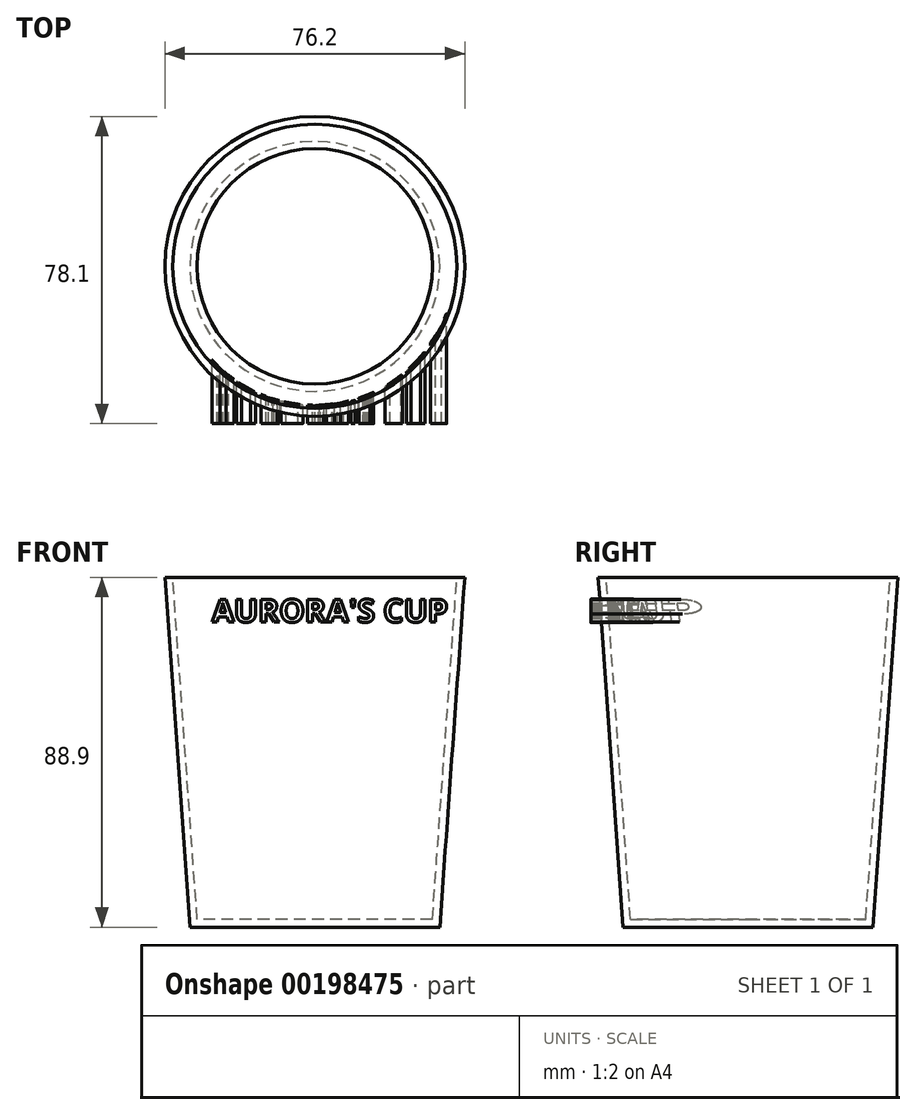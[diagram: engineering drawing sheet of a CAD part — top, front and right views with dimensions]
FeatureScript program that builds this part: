
annotation { "Feature Type Name" : "Feature", "Feature Type Description" : "" }
export const myFeature = defineFeature(function(context is Context, id is Id, definition is map)
    precondition{}
    {
        {
            var Q0;
            Q0=qCreatedBy(makeId("Top.planeOp"),FACE);
            var sketch = newSketch(context, id + "F0", { "sketchPlane" : qUnion([Q0])});
            skCircle(sketch, "E0", {"center": v(0, 0) * mm, "radius": 31.75 * mm});
            skSolve(sketch);
        }
        {
            var Q0;
            Q0=qCreatedBy(makeId("Top.planeOp"),FACE);
            cPlane(context, id + "F1", {"entities" : qUnion([Q0]), "cplaneType" : CPlaneType.OFFSET, "offset" : 88.9 * mm, "width" : 152.4 * mm, "height" : 152.4 * mm});
        }
        {
            var Q0;
            Q0=qCreatedBy(id+"F1.planeOp",FACE);
            var sketch = newSketch(context, id + "F2", { "sketchPlane" : qUnion([Q0])});
            skCircle(sketch, "E1", {"center": v(0, 0) * mm, "radius": 38.1 * mm});
            skSolve(sketch);
        }
        {
            var Q0;
            Q0 = qSketchRegion(id + "F0", true);
            var Q1;
            Q1 = qSketchRegion(id + "F2", true);
            loft(context, id + "F3", {"sheetProfilesArray" : [{ "sheetProfileEntities" : qUnion([Q0]) }, { "sheetProfileEntities" : qUnion([Q1]) }]});
        }
        {
            var Q0;
            Q0=makeQuery(id+"F3.opLoft","CAP_FACE",FACE,{"disambiguationData":[OSD([makeQuery(id+"F2.imprint","IMPRINT",FACE,{"disambiguationData":[TD([[makeQuery(id+"F2.imprint","IMPRINT",EDGE,{"derivedFrom":sQuery(id+"F2.wireOp",EDGE,"E1")}),1.0]])]})])],"isStart":true});
            shell(context, id + "F4", {"entities" : qUnion([Q0]), "thickness" : 2 * mm});
        }
        {
            var Q0;
            Q0=qCreatedBy(makeId("Front.planeOp"),FACE);
            var sketch = newSketch(context, id + "F5", { "sketchPlane" : qUnion([Q0])});
            skText(sketch, "E2", { "text": "AURORA\'S CUP", "fontName": "OpenSans-Bold.ttf"});
            const initialGuessF5  = {"E2": [-0.02616, 0.07748, 1, 0, 0.00586]};
            skSetInitialGuess(sketch, initialGuessF5);
            skSolve(sketch);
        }
        {
            var Q0;
            Q0 = qSketchRegion(id + "F5", true);
            extrude(context, id + "F6", {"entities" : qUnion([Q0]), "depth" : 40 * mm, "hasSecondDirection" : true, "secondDirectionBound" : SecondDirectionBoundingType.UP_TO_NEXT, "secondDirectionOppositeDirection" : false, "secondDirectionDepth" : 15 * mm});
        }
    });
